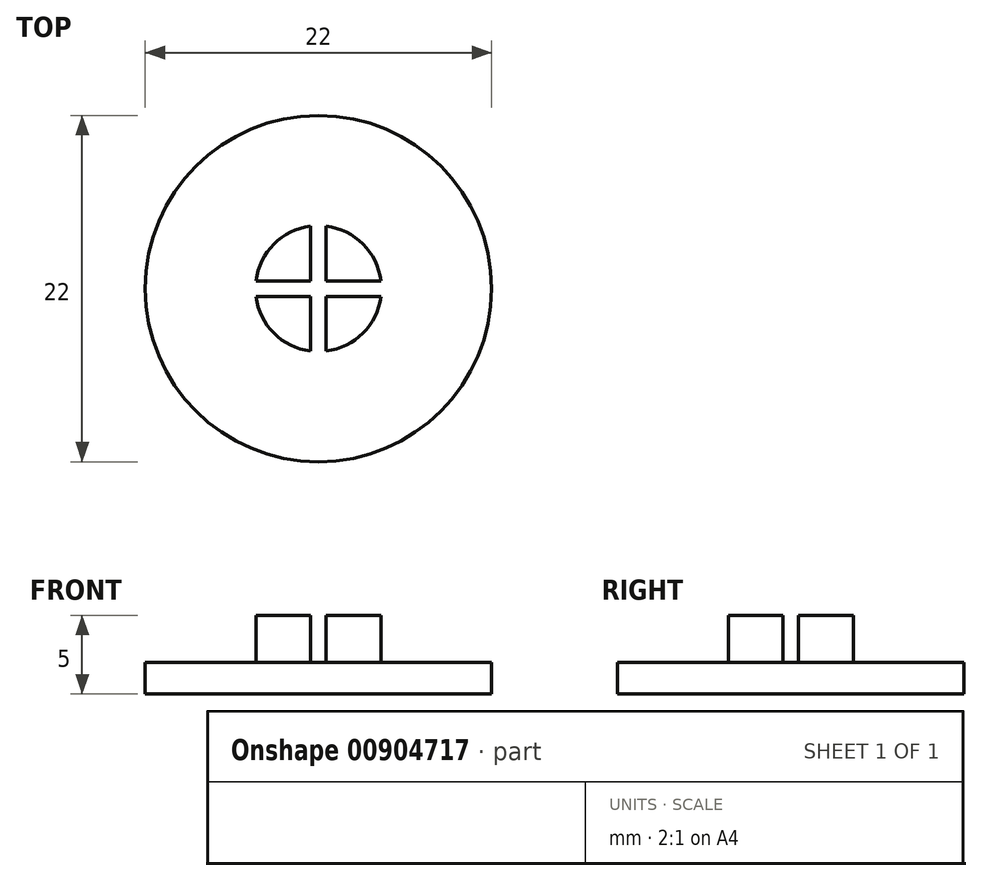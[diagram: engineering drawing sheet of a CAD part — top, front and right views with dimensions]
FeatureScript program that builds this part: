
annotation { "Feature Type Name" : "Feature", "Feature Type Description" : "" }
export const myFeature = defineFeature(function(context is Context, id is Id, definition is map)
    precondition{}
    {
        {
            var Q0;
            Q0=qCreatedBy(makeId("Top.planeOp"),FACE);
            var sketch = newSketch(context, id + "F0", { "sketchPlane" : qUnion([Q0])});
            skCircle(sketch, "E0", {"center": v(0, 0) * mm, "radius": 11 * mm});
            skSolve(sketch);
        }
        {
            var Q0;
            Q0 = qSketchRegion(id + "F0", true);
            extrude(context, id + "F1", {"entities" : qUnion([Q0]), "depth" : 2 * mm, "offsetDistance" : 25.4 * mm});
        }
        {
            var Q0;
            Q0=makeQuery(id+"F1.opExtrude","CAP_FACE",FACE,{"disambiguationData":[OSD([sQuery(id+"F0.wireOp",EDGE,"E0")])],"isStart":false});
            var sketch = newSketch(context, id + "F2", { "sketchPlane" : qUnion([Q0])});
            skArc(sketch, "E1", {"start": v(3.97, 0.5) * mm, "mid": v(2.83, 2.83) * mm, "end": v(0.5, 3.97) * mm});
            skLineSegment(sketch, "E2.bottom", {"start": v(0.5, 0.5) * mm, "end": v(3.97, 0.5) * mm});
            skLineSegment(sketch, "E2.left", {"start": v(0.5, 0.5) * mm, "end": v(0.5, 3.97) * mm});
            skSolve(sketch);
        }
        {
            var Q0;
            Q0 = qSketchRegion(id + "F2", true);
            extrude(context, id + "F3", {"entities" : qUnion([Q0]), "operationType" : NewBodyOperationType.ADD, "depth" : 3 * mm, "offsetDistance" : 25.4 * mm});
        }
        {
            var Q0;
            Q0=makeQuery(id+"F1.opExtrude","SWEPT_BODY",BODY,{"disambiguationData":[OSD([sQuery(id+"F0.wireOp",EDGE,"E0")])]});
            var Q1;
            Q1=qCreatedBy(makeId("Front.planeOp"),FACE);
            mirror(context, id + "F4", {"entities" : qUnion([Q0]), "mirrorPlane" : qUnion([Q1])});
        }
        {
            var Q0;
            Q0=makeQuery(id+"F1.opExtrude","SWEPT_BODY",BODY,{"disambiguationData":[OSD([sQuery(id+"F0.wireOp",EDGE,"E0")])]});
            var Q1;
            Q1=makeQuery(id+"F4.opPattern","COPY",BODY,{"derivedFrom":makeQuery(id+"F1.opExtrude","SWEPT_BODY",BODY,{"disambiguationData":[OSD([sQuery(id+"F0.wireOp",EDGE,"E0")])]}),"instanceName":"1"});
            var Q2;
            Q2=qCreatedBy(makeId("Right.planeOp"),FACE);
            mirror(context, id + "F5", {"entities" : qUnion([Q0, Q1]), "mirrorPlane" : qUnion([Q2])});
        }
    });
